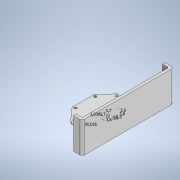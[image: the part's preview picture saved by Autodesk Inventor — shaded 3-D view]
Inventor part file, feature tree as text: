
AUTODESK INVENTOR PART (.ipt)
format: ipt  version: 2020.4 (Build 244396000, 396)  size: 345,600 bytes
history: native  units: in
note: dims shown in document units (in); Inventor stores cm internally (conversion verified against a paired STEP export)
features: extrude x10, sketch x6, fillet x2, hole x1, chamfer x1
ambient origin geometry x8: Origin, YZ Plane, XZ Plane, XY Plane, X Axis, Y Axis, Z Axis, Center Point
bodies: Solid1 (feature_tree)
feature tree (20):
  extrude  "Extrusion1"  Depth=1.2598in
  hole  "Hole1"  [1 undecoded]
  extrude  "Extrusion2"  Depth=0.1575in
  chamfer  "Chamfer1"  Distance=2.9921in
  fillet  "Fillet1"  Radius=2.874in
  fillet  "Fillet2"  Radius=0.7874in
  extrude  "Extrusion16"  Depth=0.1575in TaperAngle=0.0deg
  extrude  "Extrusion19"  Depth=1.3386in
  extrude  "Extrusion21"  Depth=0.0236in
  extrude  "Extrusion22"  Depth=0.0236in
  extrude  "Extrusion23"  Depth=0.1575in
  sketch  "Sketch12"  dims[d17=2.6772in d18=2.9921in d19=2.874in d21=0.7874in d22=0.1575in d23=0.0in d24=0.1575in d25=0.2362in d26=0.1575in d27=0.0787in d28=90.0deg d29=0.315in d30=0.8108in d31=1.3386in d33=0.7874in d34=0.6299in d35=0.1575in d36=0.6299in d37=0.1575in d38=0.7874in d39=1.3386in d40=2.9921in d41=2.0866in d42=5.5118in d43=0.1654in d45=1.811in d46=0.0in d47=0.1575in d48=0.0in d49=0.0787in d50=0.0787in d51=45.0deg d52=2.7559in d53=0.3937in d54=0.3937in d55=0.0787in d56=0.0787in d467=0.1457in d468=0.1457in d469=0.4921in d470=0.1417in d471=0.1417in d472=0.0803in d473=0.1417in d474=0.8661in d475=0.1417in d476=0.0236in d477=0.0in d482=0.0118in d483=0.0in d493=0.2818in d494=0.3881in d495=0.1063in d496=0.1053in d497=0.1979in d498=0.7745in d499=0.3268in d500=0.563in d501=0.0709in d502=0.0709in d503=0.0984in d504=0.0984in d505=0.7756in d506=0.0434in d507=0.0434in d509=0.5961in d510=0.1307in d511=0.1063in d513=0.1601in d514=0.1601in d516=0.2357in d517=0.7756in d518=0.5961in d519=1.2469in d520=0.7745in d521=0.1926in d522=0.2357in d523=1.1821in d524=0.0472in d525=0.0in d526=0.0472in d527=0.0in d528=0.0354in d529=0.0in d530=0.0354in d531=0.0in d532=0.0118in d533=0.0in d534=0.0236in d535=0.0in d44=0.0148in d443=0.0197in d444=0.0344in d445=0.0197in d446=0.0344in d449=0.0197in d450=0.0344in d451=0.0197in d452=0.0344in d453=0.0197in d454=0.0344in d457=0.0197in d458=0.0344in d459=0.0197in d460=0.0344in d461=0.0197in d462=0.0344in d463=0.0197in d464=0.0344in]
  extrude  "Extrusion24"  Depth=0.0236in
  extrude  "Extrusion25"  Depth=0.1575in
  extrude  "Extrusion26"  Depth=0.0236in
  sketch  "Sketch1"  dims[d1=1.3386in d2=1.2598in]
  sketch  "Sketch2"  dims[d3=0.6299in d4=0.6299in]
  sketch  "Sketch3"  dims[d6=0.315in d12=0.1575in]
  sketch  "Sketch10"  dims[d13=0.1575in]
  sketch  "Sketch11"  dims[d15=0.1575in]
note: 1 required parameter value undecoded (feature->parameter linkage not recoverable at this tier; creation-order binding heuristic only, values carry confidence <= 0.55)
